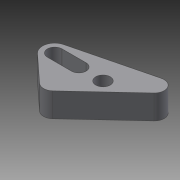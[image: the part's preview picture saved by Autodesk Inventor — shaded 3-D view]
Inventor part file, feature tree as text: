
AUTODESK INVENTOR PART (.ipt)
format: ipt  version: 2018 (Build 220112000, 112)  size: 102,912 bytes
history: native  units: mm
features: extrude x3, sketch x3, other x1
ambient origin geometry x8: Origin, YZ Plane, XZ Plane, XY Plane, X Axis, Y Axis, Z Axis, Center Point
bodies: Body1 (feature_tree)
feature tree (7):
  other  "ソリッド1"
  extrude  "押し出し1"  Depth=2.0mm
  extrude  "押し出し3"  Depth=6.5mm TaperAngle=0.0deg
  extrude  "押し出し5"  Depth=3.0mm
  sketch  "スケッチ1"
  sketch  "スケッチ3"
  sketch  "スケッチ5"
